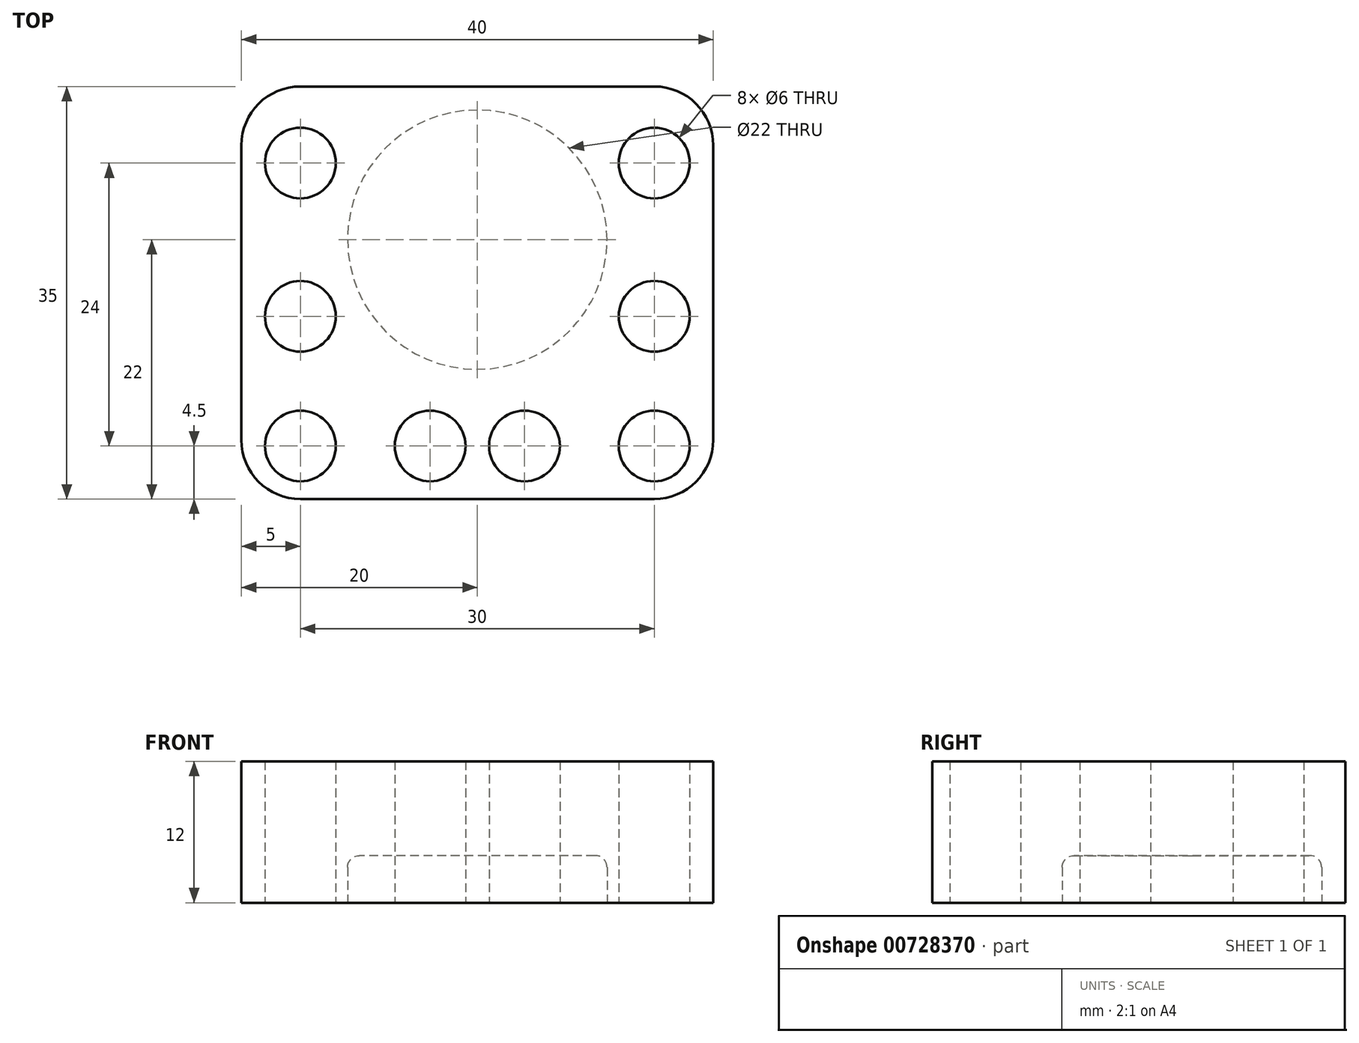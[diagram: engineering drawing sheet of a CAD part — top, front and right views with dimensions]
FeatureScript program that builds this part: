
annotation { "Feature Type Name" : "Feature", "Feature Type Description" : "" }
export const myFeature = defineFeature(function(context is Context, id is Id, definition is map)
    precondition{}
    {
        {
            var Q0;
            Q0=qCreatedBy(makeId("Top.planeOp"),FACE);
            var sketch = newSketch(context, id + "F0", { "sketchPlane" : qUnion([Q0])});
            skLineSegment(sketch, "E0.bottom", {"start": v(0, 0) * mm, "end": v(40, 0) * mm});
            skLineSegment(sketch, "E0.top", {"start": v(0, -26) * mm, "end": v(40, -26) * mm});
            skLineSegment(sketch, "E0.left", {"start": v(0, 0) * mm, "end": v(0, -13) * mm});
            skLineSegment(sketch, "E0.right", {"start": v(40, 0) * mm, "end": v(40, -13) * mm});
            skPoint(sketch, "E1", {"position": v(20, 0) * mm});
            skPoint(sketch, "E2", {"position": v(0, -13) * mm});
            skCircle(sketch, "E3", {"center": v(20, -13) * mm, "radius": 11 * mm});
            skLineSegment(sketch, "E4.top", {"start": v(0, -35) * mm, "end": v(40, -35) * mm});
            skLineSegment(sketch, "E4.left", {"start": v(0, -26) * mm, "end": v(0, -35) * mm});
            skLineSegment(sketch, "E4.right", {"start": v(40, -26) * mm, "end": v(40, -35) * mm});
            skLineSegment(sketch, "E5", {"start": v(0, -13) * mm, "end": v(0, -26) * mm});
            skPoint(sketch, "E6", {"position": v(40, -13) * mm});
            skLineSegment(sketch, "E7", {"start": v(40, -13) * mm, "end": v(40, -26) * mm});
            skPoint(sketch, "E8", {"position": v(40, -6.5) * mm});
            skPoint(sketch, "E9", {"position": v(0, -6.5) * mm});
            skPoint(sketch, "E10", {"position": v(0, -19.5) * mm});
            skPoint(sketch, "E11", {"position": v(40, -19.5) * mm});
            skCircle(sketch, "E12", {"center": v(5, -19.5) * mm, "radius": 3 * mm});
            skCircle(sketch, "E13", {"center": v(5, -6.5) * mm, "radius": 3 * mm});
            skCircle(sketch, "E14", {"center": v(35, -6.5) * mm, "radius": 3 * mm});
            skCircle(sketch, "E15", {"center": v(35, -19.5) * mm, "radius": 3 * mm});
            skCircle(sketch, "E16", {"center": v(5, -30.5) * mm, "radius": 3 * mm});
            skPoint(sketch, "E17", {"position": v(0, -30.5) * mm});
            skPoint(sketch, "E18", {"position": v(40, -30.5) * mm});
            skCircle(sketch, "E19", {"center": v(35, -30.5) * mm, "radius": 3 * mm});
            skCircle(sketch, "E20", {"center": v(16, -30.5) * mm, "radius": 3 * mm});
            skCircle(sketch, "E21", {"center": v(24, -30.5) * mm, "radius": 3 * mm});
            skSolve(sketch);
        }
        {
            var Q0;
            Q0=makeQuery(id+"F0.imprint","IMPRINT",FACE,{"disambiguationData":[TD([[makeQuery(id+"F0.imprint","IMPRINT",EDGE,{"derivedFrom":sQuery(id+"F0.wireOp",EDGE,"E0.bottom")}),-1.0]])]});
            var Q1;
            Q1=makeQuery(id+"F0.imprint","IMPRINT",FACE,{"disambiguationData":[TD([[makeQuery(id+"F0.imprint","IMPRINT",EDGE,{"derivedFrom":sQuery(id+"F0.wireOp",EDGE,"E3")}),1.0]])]});
            var Q2;
            Q2=makeQuery(id+"F0.imprint","IMPRINT",FACE,{"disambiguationData":[TD([[makeQuery(id+"F0.imprint","IMPRINT",EDGE,{"derivedFrom":sQuery(id+"F0.wireOp",EDGE,"E0.top")}),-1.0]])]});
            extrude(context, id + "F1", {"entities" : qUnion([Q0, Q1, Q2]), "depth" : 12 * mm, "offsetDistance" : 25 * mm});
        }
        {
            var Q0;
            Q0=makeQuery(id+"F0.imprint","IMPRINT",FACE,{"disambiguationData":[TD([[makeQuery(id+"F0.imprint","IMPRINT",EDGE,{"derivedFrom":sQuery(id+"F0.wireOp",EDGE,"E3")}),1.0]])]});
            extrude(context, id + "F2", {"entities" : qUnion([Q0]), "operationType" : NewBodyOperationType.REMOVE, "depth" : 4 * mm, "offsetDistance" : 25 * mm});
        }
        {
            var Q0;
            Q0=makeQuery(id+"F1.opExtrude","SWEPT_EDGE",EDGE,{"disambiguationData":[OSD([sQuery(id+"F0.wireOp",EDGE,"E4.top"),sQuery(id+"F0.wireOp",EDGE,"E4.right")])]});
            var Q1;
            Q1=makeQuery(id+"F1.opExtrude","SWEPT_EDGE",EDGE,{"disambiguationData":[OSD([sQuery(id+"F0.wireOp",EDGE,"E4.top"),sQuery(id+"F0.wireOp",EDGE,"E4.left")])]});
            var Q2;
            Q2=makeQuery(id+"F1.opExtrude","SWEPT_EDGE",EDGE,{"disambiguationData":[OSD([sQuery(id+"F0.wireOp",EDGE,"E0.bottom"),sQuery(id+"F0.wireOp",EDGE,"E0.left")])]});
            var Q3;
            Q3=makeQuery(id+"F1.opExtrude","SWEPT_EDGE",EDGE,{"disambiguationData":[OSD([sQuery(id+"F0.wireOp",EDGE,"E0.bottom"),sQuery(id+"F0.wireOp",EDGE,"E0.right")])]});
            fillet(context, id + "F3", {"entities" : qUnion([Q0, Q1, Q2, Q3]), "radius" : 5 * mm, "tangentPropagation" : true, "allowEdgeOverflow" : false});
        }
        {
            var Q0;
            Q0=makeQuery(id+"F2.boolean.opBoolean","COPY",EDGE,{"derivedFrom":makeQuery(id+"F2.opExtrude","CAP_EDGE",EDGE,{"disambiguationData":[OSD([sQuery(id+"F0.wireOp",EDGE,"E3")])],"isStart":false})});
            var Q1;
            Q1=makeQuery(id+"F2.boolean.opBoolean","COPY",EDGE,{"derivedFrom":makeQuery(id+"F2.opExtrude","CAP_EDGE",EDGE,{"disambiguationData":[OSD([sQuery(id+"F0.wireOp",EDGE,"E3")])],"isStart":true})});
            fillet(context, id + "F4", {"entities" : qUnion([Q0, Q1]), "radius" : 1 * mm, "tangentPropagation" : true, "allowEdgeOverflow" : false});
        }
    });
